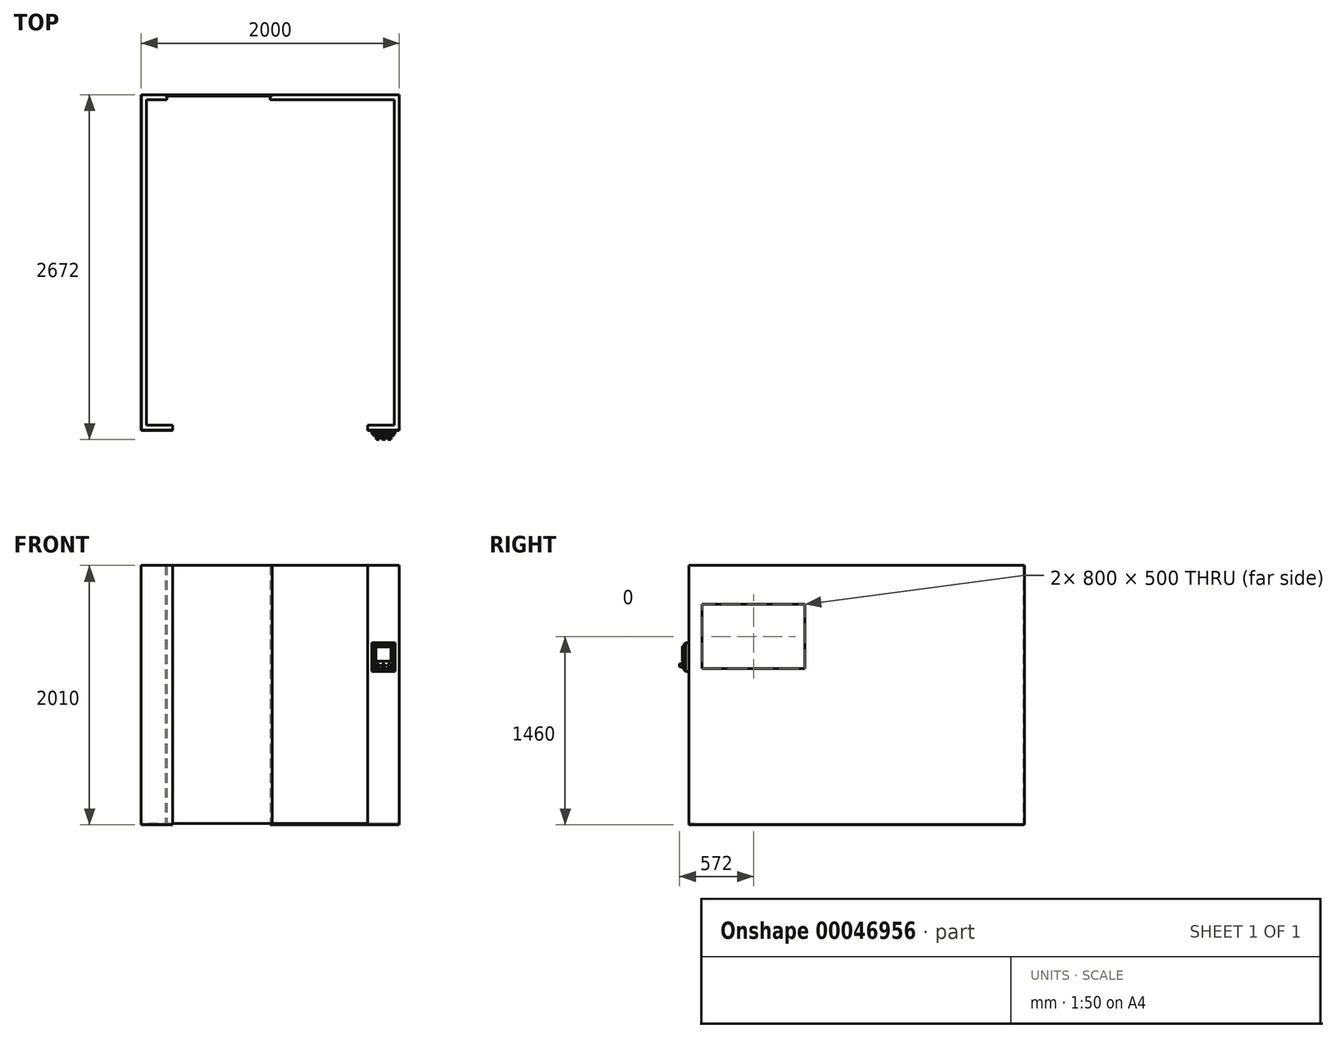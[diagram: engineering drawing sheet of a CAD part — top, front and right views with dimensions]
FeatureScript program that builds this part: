
annotation { "Feature Type Name" : "Feature", "Feature Type Description" : "" }
export const myFeature = defineFeature(function(context is Context, id is Id, definition is map)
    precondition{}
    {
        {
            var Q0;
            Q0=qCreatedBy(makeId("Top.planeOp"),FACE);
            var sketch = newSketch(context, id + "F0", { "sketchPlane" : qUnion([Q0])});
            skLineSegment(sketch, "E0", {"start": v(0, 0) * mm, "end": v(-755, 0) * mm, "construction": true});
            skLineSegment(sketch, "E1.MirrorCS", {"start": v(0, 0) * mm, "end": v(755, 0) * mm, "construction": true});
            skLineSegment(sketch, "E2", {"start": v(-755, 0) * mm, "end": v(-755, -20) * mm});
            skLineSegment(sketch, "E3", {"start": v(-755, -20) * mm, "end": v(-1000, -20) * mm});
            skLineSegment(sketch, "E4", {"start": v(-1000, -20) * mm, "end": v(-1000, 0) * mm});
            skLineSegment(sketch, "E5.MirrorCS", {"start": v(-755, 0) * mm, "end": v(-755, 20) * mm});
            skLineSegment(sketch, "E6.MirrorCS", {"start": v(-1000, 20) * mm, "end": v(-1000, 0) * mm});
            skLineSegment(sketch, "E7.MirrorCS", {"start": v(-755, 20) * mm, "end": v(-960, 20) * mm});
            skLineSegment(sketch, "E8.MirrorCS", {"start": v(755, 0) * mm, "end": v(755, -20) * mm});
            skLineSegment(sketch, "E9.MirrorCS", {"start": v(755, 0) * mm, "end": v(755, 20) * mm});
            skLineSegment(sketch, "E10.MirrorCS", {"start": v(1000, 20) * mm, "end": v(1000, 0) * mm});
            skLineSegment(sketch, "E11.MirrorCS", {"start": v(1000, -20) * mm, "end": v(1000, 0) * mm});
            skLineSegment(sketch, "E12.MirrorCS", {"start": v(755, 20) * mm, "end": v(960, 20) * mm});
            skLineSegment(sketch, "E13.MirrorCS", {"start": v(755, -20) * mm, "end": v(1000, -20) * mm});
            skLineSegment(sketch, "E14.left", {"start": v(-1000, 20) * mm, "end": v(-1000, 2540) * mm});
            skLineSegment(sketch, "E14.right", {"start": v(-960, 20) * mm, "end": v(-960, 2540) * mm});
            skLineSegment(sketch, "E15.MirrorCS", {"start": v(1000, 20) * mm, "end": v(1000, 2540) * mm});
            skLineSegment(sketch, "E16.MirrorCS", {"start": v(960, 20) * mm, "end": v(960, 2540) * mm});
            skLineSegment(sketch, "E17.bottom", {"start": v(-960, 2540) * mm, "end": v(-800, 2540) * mm});
            skLineSegment(sketch, "E17.top", {"start": v(-1000, 2580) * mm, "end": v(-800, 2580) * mm});
            skLineSegment(sketch, "E17.left", {"start": v(-1000, 2540) * mm, "end": v(-1000, 2580) * mm});
            skLineSegment(sketch, "E17.right", {"start": v(-800, 2540) * mm, "end": v(-800, 2580) * mm});
            skLineSegment(sketch, "E18.bottom", {"start": v(960, 2540) * mm, "end": v(0, 2540) * mm});
            skLineSegment(sketch, "E18.top", {"start": v(1000, 2580) * mm, "end": v(0, 2580) * mm});
            skLineSegment(sketch, "E18.left", {"start": v(1000, 2540) * mm, "end": v(1000, 2580) * mm});
            skLineSegment(sketch, "E18.right", {"start": v(0, 2540) * mm, "end": v(0, 2580) * mm});
            skSolve(sketch);
        }
        {
            var Q0;
            Q0=qSketchRegion(id+"F0",true);
            extrude(context, id + "F1", {"entities" : qUnion([Q0]), "depth" : 10 * mm});
        }
        {
            var Q0;
            Q0=makeQuery(id+"F1.opExtrude","CAP_FACE",FACE,{"disambiguationData":[OSD([sQuery(id+"F0.wireOp",EDGE,"E2"),sQuery(id+"F0.wireOp",EDGE,"E3"),sQuery(id+"F0.wireOp",EDGE,"E4"),sQuery(id+"F0.wireOp",EDGE,"E5.MirrorCS"),sQuery(id+"F0.wireOp",EDGE,"E6.MirrorCS"),sQuery(id+"F0.wireOp",EDGE,"E7.MirrorCS"),sQuery(id+"F0.wireOp",EDGE,"E14.left"),sQuery(id+"F0.wireOp",EDGE,"E14.right"),sQuery(id+"F0.wireOp",EDGE,"E17.bottom"),sQuery(id+"F0.wireOp",EDGE,"E17.top"),sQuery(id+"F0.wireOp",EDGE,"E17.left"),sQuery(id+"F0.wireOp",EDGE,"E17.right")])],"isStart":false});
            var sketch = newSketch(context, id + "F2", { "sketchPlane" : qUnion([Q0])});
            skLineSegment(sketch, "E19", {"start": v(-800, 2580) * mm, "end": v(-1000, 2580) * mm});
            skLineSegment(sketch, "E20", {"start": v(-1000, 2580) * mm, "end": v(-1000, -20) * mm});
            skLineSegment(sketch, "E21", {"start": v(-1000, -20) * mm, "end": v(-755, -20) * mm});
            skLineSegment(sketch, "E22", {"start": v(-755, -20) * mm, "end": v(-755, -18) * mm});
            skLineSegment(sketch, "E23", {"start": v(-755, -18) * mm, "end": v(-998, -18) * mm});
            skLineSegment(sketch, "E24", {"start": v(-998, -18) * mm, "end": v(-998, 2578) * mm});
            skLineSegment(sketch, "E25", {"start": v(-998, 2578) * mm, "end": v(-800, 2578) * mm});
            skLineSegment(sketch, "E26", {"start": v(-800, 2578) * mm, "end": v(-800, 2580) * mm});
            skSolve(sketch);
        }
        {
            var Q0;
            Q0=qSketchRegion(id+"F2",true);
            extrude(context, id + "F3", {"entities" : qUnion([Q0]), "operationType" : NewBodyOperationType.ADD, "depth" : 2000 * mm});
        }
        {
            var Q0;
            Q0=makeQuery(id+"F1.opExtrude","CAP_FACE",FACE,{"disambiguationData":[OSD([sQuery(id+"F0.wireOp",EDGE,"E8.MirrorCS"),sQuery(id+"F0.wireOp",EDGE,"E9.MirrorCS"),sQuery(id+"F0.wireOp",EDGE,"E11.MirrorCS"),sQuery(id+"F0.wireOp",EDGE,"E12.MirrorCS"),sQuery(id+"F0.wireOp",EDGE,"E13.MirrorCS"),sQuery(id+"F0.wireOp",EDGE,"E10.MirrorCS"),sQuery(id+"F0.wireOp",EDGE,"E15.MirrorCS"),sQuery(id+"F0.wireOp",EDGE,"E16.MirrorCS"),sQuery(id+"F0.wireOp",EDGE,"E18.bottom"),sQuery(id+"F0.wireOp",EDGE,"E18.top"),sQuery(id+"F0.wireOp",EDGE,"E18.left"),sQuery(id+"F0.wireOp",EDGE,"E18.right")])],"isStart":false});
            var sketch = newSketch(context, id + "F4", { "sketchPlane" : qUnion([Q0])});
            skLineSegment(sketch, "E27", {"start": v(0, 2580) * mm, "end": v(1000, 2580) * mm});
            skLineSegment(sketch, "E28", {"start": v(1000, 2580) * mm, "end": v(1000, -20) * mm});
            skLineSegment(sketch, "E29", {"start": v(1000, -20) * mm, "end": v(755, -20) * mm});
            skLineSegment(sketch, "E30", {"start": v(755, -20) * mm, "end": v(755, -18) * mm});
            skLineSegment(sketch, "E31", {"start": v(755, -18) * mm, "end": v(998, -18) * mm});
            skLineSegment(sketch, "E32", {"start": v(998, -18) * mm, "end": v(998, 2578) * mm});
            skLineSegment(sketch, "E33", {"start": v(998, 2578) * mm, "end": v(0, 2578) * mm});
            skLineSegment(sketch, "E34", {"start": v(0, 2578) * mm, "end": v(0, 2580) * mm});
            skSolve(sketch);
        }
        {
            var Q0;
            Q0=qSketchRegion(id+"F4",true);
            extrude(context, id + "F5", {"entities" : qUnion([Q0]), "operationType" : NewBodyOperationType.ADD, "depth" : 2000 * mm});
        }
        {
            var Q0;
            Q0=makeQuery(id+"F5.boolean.opBoolean","MERGE",FACE,{"derivedFrom":[makeQuery(id+"F1.opExtrude","SWEPT_FACE",FACE,{"disambiguationData":[OSD([sQuery(id+"F0.wireOp",EDGE,"E18.top")])]}),makeQuery(id+"F5.opExtrude","SWEPT_FACE",FACE,{"disambiguationData":[OSD([sQuery(id+"F4.wireOp",EDGE,"E27")])]})]});
            var sketch = newSketch(context, id + "F6", { "sketchPlane" : qUnion([Q0])});
            skLineSegment(sketch, "E35.bottom", {"start": v(-15, 2010) * mm, "end": v(815, 2010) * mm});
            skLineSegment(sketch, "E35.top", {"start": v(-15, 10) * mm, "end": v(815, 10) * mm});
            skLineSegment(sketch, "E35.left", {"start": v(-15, 2010) * mm, "end": v(-15, 10) * mm});
            skLineSegment(sketch, "E35.right", {"start": v(815, 2010) * mm, "end": v(815, 10) * mm});
            skSolve(sketch);
        }
        {
            var Q0;
            Q0=qSketchRegion(id+"F6",true);
            extrude(context, id + "F7", {"entities" : qUnion([Q0]), "oppositeDirection" : true, "depth" : 10 * mm});
        }
        {
            var Q0;
            Q0=makeQuery(id+"F5.boolean.opBoolean","MERGE",FACE,{"derivedFrom":[makeQuery(id+"F1.opExtrude","SWEPT_FACE",FACE,{"disambiguationData":[OSD([sQuery(id+"F0.wireOp",EDGE,"E11.MirrorCS"),sQuery(id+"F0.wireOp",EDGE,"E10.MirrorCS"),sQuery(id+"F0.wireOp",EDGE,"E15.MirrorCS"),sQuery(id+"F0.wireOp",EDGE,"E18.left")])]}),makeQuery(id+"F5.opExtrude","SWEPT_FACE",FACE,{"disambiguationData":[OSD([sQuery(id+"F4.wireOp",EDGE,"E28")])]})]});
            var sketch = newSketch(context, id + "F8", { "sketchPlane" : qUnion([Q0])});
            skLineSegment(sketch, "E36.bottom", {"start": v(80, 1710) * mm, "end": v(880, 1710) * mm});
            skLineSegment(sketch, "E36.top", {"start": v(80, 1210) * mm, "end": v(880, 1210) * mm});
            skLineSegment(sketch, "E36.left", {"start": v(80, 1710) * mm, "end": v(80, 1210) * mm});
            skLineSegment(sketch, "E36.right", {"start": v(880, 1710) * mm, "end": v(880, 1210) * mm});
            skSolve(sketch);
        }
        {
            var Q0;
            Q0=qSketchRegion(id+"F8",true);
            extrude(context, id + "F9", {"entities" : qUnion([Q0]), "operationType" : NewBodyOperationType.REMOVE, "oppositeDirection" : true, "depth" : 5 * mm});
        }
        {
            var Q0;
            Q0=makeQuery(id+"F3.boolean.opBoolean","MERGE",FACE,{"derivedFrom":[makeQuery(id+"F1.opExtrude","SWEPT_FACE",FACE,{"disambiguationData":[OSD([sQuery(id+"F0.wireOp",EDGE,"E4"),sQuery(id+"F0.wireOp",EDGE,"E6.MirrorCS"),sQuery(id+"F0.wireOp",EDGE,"E14.left"),sQuery(id+"F0.wireOp",EDGE,"E17.left")])]}),makeQuery(id+"F3.opExtrude","SWEPT_FACE",FACE,{"disambiguationData":[OSD([sQuery(id+"F2.wireOp",EDGE,"E20")])]})]});
            var sketch = newSketch(context, id + "F10", { "sketchPlane" : qUnion([Q0])});
            skLineSegment(sketch, "E37.bottom", {"start": v(-880, 1710) * mm, "end": v(-80, 1710) * mm});
            skLineSegment(sketch, "E37.top", {"start": v(-880, 1210) * mm, "end": v(-80, 1210) * mm});
            skLineSegment(sketch, "E37.left", {"start": v(-880, 1710) * mm, "end": v(-880, 1210) * mm});
            skLineSegment(sketch, "E37.right", {"start": v(-80, 1710) * mm, "end": v(-80, 1210) * mm});
            skSolve(sketch);
        }
        {
            var Q0;
            Q0=qSketchRegion(id+"F10",true);
            extrude(context, id + "F11", {"entities" : qUnion([Q0]), "operationType" : NewBodyOperationType.REMOVE, "oppositeDirection" : true, "depth" : 5 * mm});
        }
        {
            var Q0;
            Q0=makeQuery(id+"F3.boolean.opBoolean","MERGE",FACE,{"derivedFrom":[makeQuery(id+"F1.opExtrude","SWEPT_FACE",FACE,{"disambiguationData":[OSD([sQuery(id+"F0.wireOp",EDGE,"E4"),sQuery(id+"F0.wireOp",EDGE,"E6.MirrorCS"),sQuery(id+"F0.wireOp",EDGE,"E14.left"),sQuery(id+"F0.wireOp",EDGE,"E17.left")])]}),makeQuery(id+"F3.opExtrude","SWEPT_FACE",FACE,{"disambiguationData":[OSD([sQuery(id+"F2.wireOp",EDGE,"E20")])]})]});
            var sketch = newSketch(context, id + "F12", { "sketchPlane" : qUnion([Q0])});
            skLineSegment(sketch, "E38.bottom", {"start": v(-880, 1710) * mm, "end": v(-80, 1710) * mm});
            skLineSegment(sketch, "E38.top", {"start": v(-880, 1210) * mm, "end": v(-80, 1210) * mm});
            skLineSegment(sketch, "E38.left", {"start": v(-880, 1710) * mm, "end": v(-880, 1210) * mm});
            skLineSegment(sketch, "E38.right", {"start": v(-80, 1710) * mm, "end": v(-80, 1210) * mm});
            skSolve(sketch);
        }
        {
            var Q0;
            Q0=qSketchRegion(id+"F12",true);
            extrude(context, id + "F13", {"entities" : qUnion([Q0]), "oppositeDirection" : true, "depth" : 2 * mm});
        }
        {
            var Q0;
            Q0=makeQuery(id+"F5.boolean.opBoolean","MERGE",FACE,{"derivedFrom":[makeQuery(id+"F1.opExtrude","SWEPT_FACE",FACE,{"disambiguationData":[OSD([sQuery(id+"F0.wireOp",EDGE,"E11.MirrorCS"),sQuery(id+"F0.wireOp",EDGE,"E10.MirrorCS"),sQuery(id+"F0.wireOp",EDGE,"E15.MirrorCS"),sQuery(id+"F0.wireOp",EDGE,"E18.left")])]}),makeQuery(id+"F5.opExtrude","SWEPT_FACE",FACE,{"disambiguationData":[OSD([sQuery(id+"F4.wireOp",EDGE,"E28")])]})]});
            var sketch = newSketch(context, id + "F14", { "sketchPlane" : qUnion([Q0])});
            skLineSegment(sketch, "E39.bottom", {"start": v(80, 1710) * mm, "end": v(880, 1710) * mm});
            skLineSegment(sketch, "E39.top", {"start": v(80, 1210) * mm, "end": v(880, 1210) * mm});
            skLineSegment(sketch, "E39.left", {"start": v(80, 1710) * mm, "end": v(80, 1210) * mm});
            skLineSegment(sketch, "E39.right", {"start": v(880, 1710) * mm, "end": v(880, 1210) * mm});
            skSolve(sketch);
        }
        {
            var Q0;
            Q0=qSketchRegion(id+"F14",true);
            extrude(context, id + "F15", {"entities" : qUnion([Q0]), "oppositeDirection" : true, "depth" : 2 * mm});
        }
        {
            var Q0;
            Q0=makeQuery(id+"F3.opExtrude","SWEPT_FACE",FACE,{"disambiguationData":[OSD([sQuery(id+"F2.wireOp",EDGE,"E25")])]});
            var sketch = newSketch(context, id + "F16", { "sketchPlane" : qUnion([Q0])});
            skLineSegment(sketch, "E40", {"start": v(-800, 10) * mm, "end": v(-815, 10) * mm});
            skPoint(sketch, "E41", {"position": v(-815, 10) * mm});
            skSolve(sketch);
        }
        {
            var Q0;
            Q0=makeQuery(id+"F5.boolean.opBoolean","MERGE",FACE,{"derivedFrom":[makeQuery(id+"F1.opExtrude","SWEPT_FACE",FACE,{"disambiguationData":[OSD([sQuery(id+"F0.wireOp",EDGE,"E13.MirrorCS")])]}),makeQuery(id+"F5.opExtrude","SWEPT_FACE",FACE,{"disambiguationData":[OSD([sQuery(id+"F4.wireOp",EDGE,"E29")])]})]});
            var sketch = newSketch(context, id + "F17", { "sketchPlane" : qUnion([Q0])});
            skLineSegment(sketch, "E42.bottom", {"start": v(787.5, 1410) * mm, "end": v(967.5, 1410) * mm});
            skLineSegment(sketch, "E42.top", {"start": v(787.5, 1190) * mm, "end": v(967.5, 1190) * mm});
            skLineSegment(sketch, "E42.left", {"start": v(787.5, 1410) * mm, "end": v(787.5, 1190) * mm});
            skLineSegment(sketch, "E42.right", {"start": v(967.5, 1410) * mm, "end": v(967.5, 1190) * mm});
            skSolve(sketch);
        }
        {
            var Q0;
            Q0 = qSketchRegion(id + "F17", true);
            extrude(context, id + "F18", {"entities" : qUnion([Q0]), "depth" : 25 * mm});
        }
        {
            var Q0;
            Q0=makeQuery(id+"F18.opExtrude","CAP_FACE",FACE,{"disambiguationData":[OSD([sQuery(id+"F17.wireOp",EDGE,"E42.bottom"),sQuery(id+"F17.wireOp",EDGE,"E42.top"),sQuery(id+"F17.wireOp",EDGE,"E42.left"),sQuery(id+"F17.wireOp",EDGE,"E42.right")])],"isStart":false});
            cPlane(context, id + "F19", {"entities" : qUnion([Q0]), "cplaneType" : CPlaneType.OFFSET, "offset" : 20 * mm, "width" : 150 * mm, "height" : 150 * mm});
        }
        {
            var Q0;
            Q0=qCreatedBy(id+"F19.planeOp",FACE);
            var sketch = newSketch(context, id + "F20", { "sketchPlane" : qUnion([Q0])});
            skLineSegment(sketch, "E43.0", {"start": v(947.5, 1390) * mm, "end": v(947.5, 1210) * mm});
            skLineSegment(sketch, "E44.0", {"start": v(807.5, 1390) * mm, "end": v(947.5, 1390) * mm});
            skLineSegment(sketch, "E45.0", {"start": v(807.5, 1390) * mm, "end": v(807.5, 1210) * mm});
            skLineSegment(sketch, "E46.0", {"start": v(807.5, 1210) * mm, "end": v(947.5, 1210) * mm});
            skPoint(sketch, "E47.orphan", {"position": v(787.5, 1410) * mm});
            skPoint(sketch, "E48.orphan", {"position": v(787.5, 1190) * mm});
            skPoint(sketch, "E49.0.end.orphan", {"position": v(967.5, 1190) * mm});
            skPoint(sketch, "E50.0.start.orphan", {"position": v(967.5, 1410) * mm});
            skSolve(sketch);
        }
        {
            var Q0;
            Q0=makeQuery(id+"F18.opExtrude","CAP_FACE",FACE,{"disambiguationData":[OSD([sQuery(id+"F17.wireOp",EDGE,"E42.bottom"),sQuery(id+"F17.wireOp",EDGE,"E42.top"),sQuery(id+"F17.wireOp",EDGE,"E42.left"),sQuery(id+"F17.wireOp",EDGE,"E42.right")])],"isStart":false});
            var Q1;
            Q1=makeQuery(id+"F20.imprint","IMPRINT",FACE,{"disambiguationData":[TD([[makeQuery(id+"F20.imprint","IMPRINT",EDGE,{"derivedFrom":sQuery(id+"F20.wireOp",EDGE,"E43.0")}),-1.0]])]});
            var Q2;
            Q2=sQuery(id+"F20.wireOp",EDGE,"E46.0");
            var Q3;
            Q3=sQuery(id+"F20.wireOp",EDGE,"E45.0");
            var Q4;
            Q4=sQuery(id+"F20.wireOp",EDGE,"E44.0");
            var Q5;
            Q5=sQuery(id+"F20.wireOp",EDGE,"E43.0");
            loft(context, id + "F21", {"sheetProfilesArray" : [{ "sheetProfileEntities" : qUnion([Q0]) }, { "sheetProfileEntities" : qUnion([Q1]) }], "guidesArray" : [{ "guideEntities" : qUnion([Q2]), "guideDerivativeType" : LoftGuideDerivativeType.DEFAULT, "guideDerivativeMagnitude" : 1 }, { "guideEntities" : qUnion([Q3]), "guideDerivativeType" : LoftGuideDerivativeType.DEFAULT, "guideDerivativeMagnitude" : 1 }, { "guideEntities" : qUnion([Q4]), "guideDerivativeType" : LoftGuideDerivativeType.DEFAULT, "guideDerivativeMagnitude" : 1 }, { "guideEntities" : qUnion([Q5]), "guideDerivativeType" : LoftGuideDerivativeType.DEFAULT, "guideDerivativeMagnitude" : 1 }]});
        }
        {
            var Q0;
            Q0=makeQuery(id+"F21.opLoft","CAP_FACE",FACE,{"disambiguationData":[OSD([makeQuery(id+"F20.imprint","IMPRINT",FACE,{"disambiguationData":[TD([[makeQuery(id+"F20.imprint","IMPRINT",EDGE,{"derivedFrom":sQuery(id+"F20.wireOp",EDGE,"E43.0")}),-1.0]])]})])],"isStart":true});
            extrude(context, id + "F22", {"entities" : qUnion([Q0]), "endBound" : BoundingType.SYMMETRIC, "depth" : 4 * mm});
        }
        {
            var Q0;
            Q0=makeQuery(id+"F22.opExtrude","CAP_FACE",FACE,{"disambiguationData":[OSD([makeQuery(id+"F20.imprint","IMPRINT",FACE,{"disambiguationData":[TD([[makeQuery(id+"F20.imprint","IMPRINT",EDGE,{"derivedFrom":sQuery(id+"F20.wireOp",EDGE,"E43.0")}),-1.0]])]})])],"isStart":false});
            var sketch = newSketch(context, id + "F23", { "sketchPlane" : qUnion([Q0])});
            skCircle(sketch, "E51", {"center": v(877.5, 1235) * mm, "radius": 12.5 * mm});
            skPoint(sketch, "E51.centerSnap0", {"position": v(877.5, 1210) * mm});
            skCircle(sketch, "E52", {"center": v(832.5, 1235) * mm, "radius": 12.5 * mm});
            skCircle(sketch, "E53", {"center": v(922.5, 1235) * mm, "radius": 12.5 * mm});
            skLineSegment(sketch, "E54", {"start": v(877.5, 1235) * mm, "end": v(832.5, 1235) * mm, "construction": true});
            skLineSegment(sketch, "E55", {"start": v(877.5, 1235) * mm, "end": v(922.5, 1235) * mm, "construction": true});
            skSolve(sketch);
        }
        {
            var Q0;
            Q0 = qSketchRegion(id + "F23", true);
            extrude(context, id + "F24", {"entities" : qUnion([Q0]), "depth" : 25 * mm});
        }
        {
            var Q0;
            Q0=makeQuery(id+"F22.opExtrude","CAP_FACE",FACE,{"disambiguationData":[OSD([makeQuery(id+"F20.imprint","IMPRINT",FACE,{"disambiguationData":[TD([[makeQuery(id+"F20.imprint","IMPRINT",EDGE,{"derivedFrom":sQuery(id+"F20.wireOp",EDGE,"E43.0")}),-1.0]])]})])],"isStart":false});
            var sketch = newSketch(context, id + "F25", { "sketchPlane" : qUnion([Q0])});
            skLineSegment(sketch, "E56.bottom", {"start": v(935.5, 1378) * mm, "end": v(819.5, 1378) * mm});
            skLineSegment(sketch, "E56.top", {"start": v(935.5, 1268) * mm, "end": v(819.5, 1268) * mm});
            skLineSegment(sketch, "E56.left", {"start": v(935.5, 1378) * mm, "end": v(935.5, 1268) * mm});
            skLineSegment(sketch, "E56.right", {"start": v(819.5, 1378) * mm, "end": v(819.5, 1268) * mm});
            skSolve(sketch);
        }
        {
            var Q0;
            Q0 = qSketchRegion(id + "F25", true);
            var Q1;
            Q1=makeQuery(id+"F25.imprint","IMPRINT",FACE,{"disambiguationData":[TD([[makeQuery(id+"F25.imprint","IMPRINT",EDGE,{"derivedFrom":sQuery(id+"F25.wireOp",EDGE,"E56.bottom")}),1.0]])]});
            extrude(context, id + "F26", {"entities" : qUnion([Q0, Q1]), "depth" : 3 * mm});
        }
    });
